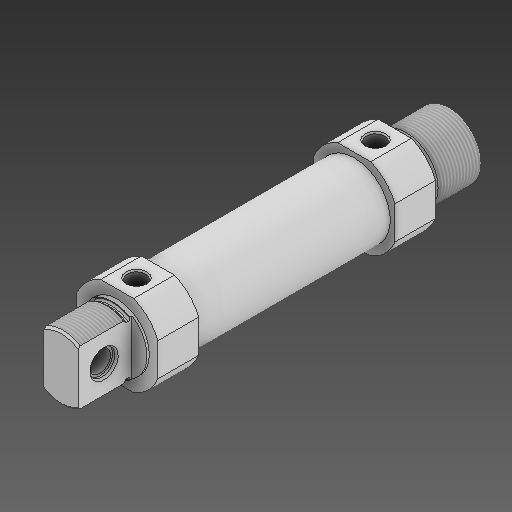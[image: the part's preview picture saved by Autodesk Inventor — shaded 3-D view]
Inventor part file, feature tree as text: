
AUTODESK INVENTOR PART (.ipt)
format: ipt  version: 2021 (Build 250183000, 183)  size: 323,584 bytes
history: native  units: in
note: dims shown in document units (in); Inventor stores cm internally (conversion verified against a paired STEP export)
features: other x78, sketch x7
ambient origin geometry x8: Origin, YZ Plane, XZ Plane, XY Plane, X Axis, Y Axis, Z Axis, Center Point
bodies: Solid1 (feature_tree)
feature tree (85):
  other  "193992 DSNU-32-60-PPS---(A----0-ZR).ipt"
  other  "Solid1::193992 DSNU-32-60-PPS---(A----0-ZR).ipt"
  other  "TaggingFeature1"
  sketch  "Sketch_12"
  sketch  "Sketch_1"  dims[d0=0.3937in]
  sketch  "Sketch_124"
  sketch  "Sketch_3"  dims[d25=0.0in d26=0.0in d27=0.0in d28=0.0in d29=0.0in d30=0.0in]
  sketch  "Sketch5"
  sketch  "Sketch6"
  sketch  "Sketch_129"
  other  "FDT_FRONT_XY"
  other  "FDT_FRONT_YZ"
  other  "FDT_FRONT_ZX"
  other  "FDT_QSFRONT_XY"
  other  "FDT_QSFRONT_YZ"
  other  "FDT_QSFRONT_ZX"
  other  "FDT_QSREAR_XY"
  other  "FDT_QSREAR_YZ"
  other  "FDT_QSREAR_ZX"
  other  "FDT_REAR_XY"
  other  "FDT_REAR_YZ"
  other  "FDT_REAR_ZX"
  other  "FDT_SMBR1_XY"
  other  "FDT_SMBR1_YZ"
  other  "FDT_SMBR1_ZX"
  other  "FDT_SMBR2_XY"
  other  "FDT_SMBR2_YZ"
  other  "FDT_SMBR2_ZX"
  other  "FDT_SWIVELAXIS_XY"
  other  "FDT_SWIVELAXIS_YZ"
  other  "FDT_SWIVELAXIS_ZX"
  other  "NUT_XY"
  other  "NUT_YZ"
  other  "NUT_ZX"
  other  "ZR_XY"
  other  "ZR_YZ"
  other  "ZR_ZX"
  other  "ZYL_XY"
  other  "ZYL_YZ"
  other  "ZYL_ZX"
  other  "FDT_FRONT_X"
  other  "FDT_FRONT_Y"
  other  "FDT_FRONT_Z"
  other  "FDT_QSFRONT_X"
  other  "FDT_QSFRONT_Y"
  other  "FDT_QSFRONT_Z"
  other  "FDT_QSREAR_X"
  other  "FDT_QSREAR_Y"
  other  "FDT_QSREAR_Z"
  other  "FDT_REAR_X"
  other  "FDT_REAR_Y"
  other  "FDT_REAR_Z"
  other  "FDT_SMBR1_X"
  other  "FDT_SMBR1_Y"
  other  "FDT_SMBR1_Z"
  other  "FDT_SMBR2_X"
  other  "FDT_SMBR2_Y"
  other  "FDT_SMBR2_Z"
  other  "FDT_SWIVELAXIS_X"
  other  "FDT_SWIVELAXIS_Y"
  other  "FDT_SWIVELAXIS_Z"
  other  "NUT_X"
  other  "NUT_Y"
  other  "NUT_Z"
  other  "ZR_X"
  other  "ZR_Y"
  other  "ZR_Z"
  other  "ZYL_X"
  other  "ZYL_Y"
  other  "ZYL_Z"
  other  "FDT_FRONT_Center"
  other  "FDT_QSFRONT_Center"
  other  "FDT_QSREAR_Center"
  other  "FDT_REAR_Center"
  other  "FDT_SMBR1_Center"
  other  "FDT_SMBR2_Center"
  other  "FDT_SWIVELAXIS_Center"
  other  "NUT_Center"
  other  "ZR_Center"
  other  "ZYL_Center"
  other  "FDT_FRONT"
  other  "FDT_REAR"
  other  "FDT_QSFRONT"
  other  "FDT_QSREAR"
  other  "ZYL"
